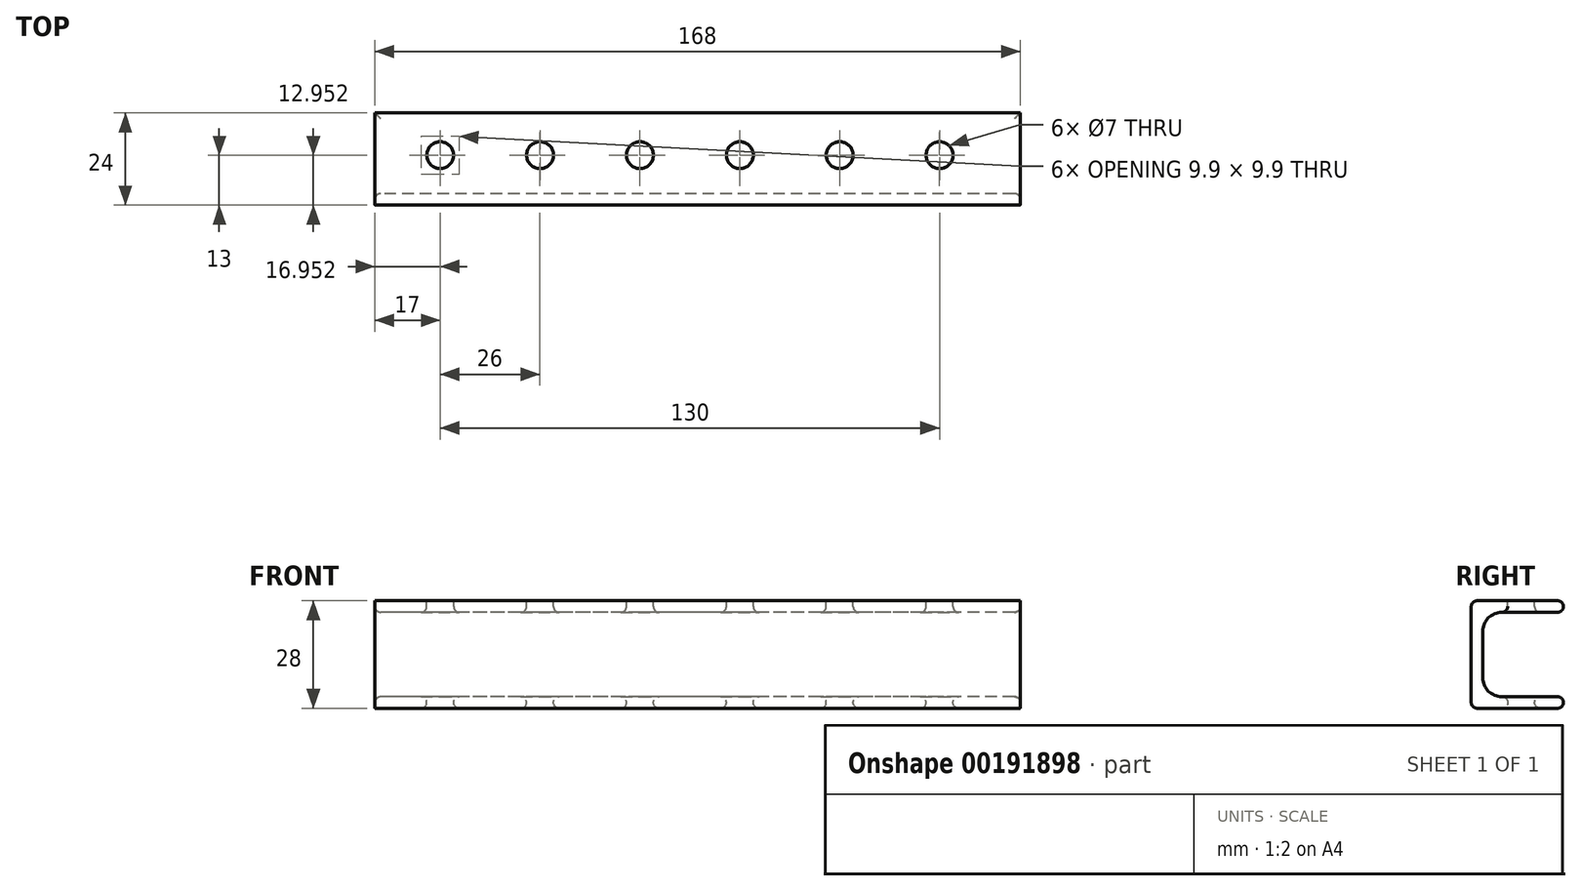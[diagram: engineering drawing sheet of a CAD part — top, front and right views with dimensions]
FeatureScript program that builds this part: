
annotation { "Feature Type Name" : "Feature", "Feature Type Description" : "" }
export const myFeature = defineFeature(function(context is Context, id is Id, definition is map)
    precondition{}
    {
        {
            var Q0;
            Q0=qCreatedBy(makeId("Right.planeOp"),FACE);
            var sketch = newSketch(context, id + "F0", { "sketchPlane" : qUnion([Q0])});
            skLineSegment(sketch, "E0", {"start": v(0, 0) * mm, "end": v(-24, 0) * mm});
            skLineSegment(sketch, "E1", {"start": v(-24, 0) * mm, "end": v(-24, 28) * mm});
            skLineSegment(sketch, "E2", {"start": v(-24, 28) * mm, "end": v(0, 28) * mm});
            skLineSegment(sketch, "E3", {"start": v(0, 28) * mm, "end": v(0, 25) * mm});
            skLineSegment(sketch, "E4", {"start": v(0, 25) * mm, "end": v(-21, 25) * mm});
            skLineSegment(sketch, "E5", {"start": v(-21, 25) * mm, "end": v(-21, 3) * mm});
            skLineSegment(sketch, "E6", {"start": v(-21, 3) * mm, "end": v(0, 3) * mm});
            skLineSegment(sketch, "E7", {"start": v(0, 3) * mm, "end": v(0, 0) * mm});
            skSolve(sketch);
        }
        {
            var Q0;
            Q0=makeQuery(id+"F0.imprint","IMPRINT",FACE,{"disambiguationData":[TD([[makeQuery(id+"F0.imprint","IMPRINT",EDGE,{"derivedFrom":sQuery(id+"F0.wireOp",EDGE,"E0")}),-1.0]])]});
            extrude(context, id + "F1", {"entities" : qUnion([Q0]), "depth" : 168 * mm});
        }
        {
            var Q0;
            Q0=makeQuery(id+"F1.opExtrude","SWEPT_FACE",FACE,{"disambiguationData":[OSD([sQuery(id+"F0.wireOp",EDGE,"E2")])]});
            var sketch = newSketch(context, id + "F2", { "sketchPlane" : qUnion([Q0])});
            skCircle(sketch, "E8", {"center": v(17, -11) * mm, "radius": 3.5 * mm});
            skCircle(sketch, "E9.1.0.0", {"center": v(43, -11) * mm, "radius": 3.5 * mm});
            skCircle(sketch, "E9.2.0.0", {"center": v(69, -11) * mm, "radius": 3.5 * mm});
            skCircle(sketch, "E9.3.0.0", {"center": v(95, -11) * mm, "radius": 3.5 * mm});
            skCircle(sketch, "E9.4.0.0", {"center": v(121, -11) * mm, "radius": 3.5 * mm});
            skCircle(sketch, "E9.5.0.0", {"center": v(147, -11) * mm, "radius": 3.5 * mm});
            skLineSegment(sketch, "E9.direction1", {"start": v(17, -11) * mm, "end": v(43, -11) * mm, "construction": true});
            skSolve(sketch);
        }
        {
            var Q0;
            Q0=makeQuery(id+"F2.imprint","IMPRINT",FACE,{"disambiguationData":[TD([[makeQuery(id+"F2.imprint","IMPRINT",EDGE,{"derivedFrom":sQuery(id+"F2.wireOp",EDGE,"E8")}),1.0]])]});
            var Q1;
            Q1=makeQuery(id+"F2.imprint","IMPRINT",FACE,{"disambiguationData":[TD([[makeQuery(id+"F2.imprint","IMPRINT",EDGE,{"derivedFrom":sQuery(id+"F2.wireOp",EDGE,"E9.1.0.0")}),1.0]])]});
            var Q2;
            Q2=makeQuery(id+"F2.imprint","IMPRINT",FACE,{"disambiguationData":[TD([[makeQuery(id+"F2.imprint","IMPRINT",EDGE,{"derivedFrom":sQuery(id+"F2.wireOp",EDGE,"E9.2.0.0")}),1.0]])]});
            var Q3;
            Q3=makeQuery(id+"F2.imprint","IMPRINT",FACE,{"disambiguationData":[TD([[makeQuery(id+"F2.imprint","IMPRINT",EDGE,{"derivedFrom":sQuery(id+"F2.wireOp",EDGE,"E9.3.0.0")}),1.0]])]});
            var Q4;
            Q4=makeQuery(id+"F2.imprint","IMPRINT",FACE,{"disambiguationData":[TD([[makeQuery(id+"F2.imprint","IMPRINT",EDGE,{"derivedFrom":sQuery(id+"F2.wireOp",EDGE,"E9.4.0.0")}),1.0]])]});
            var Q5;
            Q5=makeQuery(id+"F2.imprint","IMPRINT",FACE,{"disambiguationData":[TD([[makeQuery(id+"F2.imprint","IMPRINT",EDGE,{"derivedFrom":sQuery(id+"F2.wireOp",EDGE,"E9.5.0.0")}),1.0]])]});
            extrude(context, id + "F3", {"entities" : qUnion([Q0, Q1, Q2, Q3, Q4, Q5]), "operationType" : NewBodyOperationType.REMOVE, "oppositeDirection" : true, "depth" : 55 * mm});
        }
        {
            var Q0;
            Q0=makeQuery(id+"F1.opExtrude","SWEPT_EDGE",EDGE,{"disambiguationData":[OSD([sQuery(id+"F0.wireOp",EDGE,"E5"),sQuery(id+"F0.wireOp",EDGE,"E6")])]});
            var Q1;
            Q1=makeQuery(id+"F1.opExtrude","SWEPT_EDGE",EDGE,{"disambiguationData":[OSD([sQuery(id+"F0.wireOp",EDGE,"E4"),sQuery(id+"F0.wireOp",EDGE,"E5")])]});
            fillet(context, id + "F4", {"entities" : qUnion([Q0, Q1]), "radius" : 5 * mm, "tangentPropagation" : true, "allowEdgeOverflow" : false});
        }
        {
            var Q0;
            Q0=makeQuery(id+"F1.opExtrude","SWEPT_EDGE",EDGE,{"disambiguationData":[OSD([sQuery(id+"F0.wireOp",EDGE,"E6"),sQuery(id+"F0.wireOp",EDGE,"E7")])]});
            var Q1;
            Q1=makeQuery(id+"F1.opExtrude","SWEPT_EDGE",EDGE,{"disambiguationData":[OSD([sQuery(id+"F0.wireOp",EDGE,"E0"),sQuery(id+"F0.wireOp",EDGE,"E7")])]});
            var Q2;
            Q2=makeQuery(id+"F1.opExtrude","SWEPT_EDGE",EDGE,{"disambiguationData":[OSD([sQuery(id+"F0.wireOp",EDGE,"E2"),sQuery(id+"F0.wireOp",EDGE,"E3")])]});
            var Q3;
            Q3=makeQuery(id+"F1.opExtrude","SWEPT_EDGE",EDGE,{"disambiguationData":[OSD([sQuery(id+"F0.wireOp",EDGE,"E3"),sQuery(id+"F0.wireOp",EDGE,"E4")])]});
            var Q4;
            Q4=makeQuery(id+"F1.opExtrude","SWEPT_EDGE",EDGE,{"disambiguationData":[OSD([sQuery(id+"F0.wireOp",EDGE,"E1"),sQuery(id+"F0.wireOp",EDGE,"E2")])]});
            var Q5;
            Q5=makeQuery(id+"F1.opExtrude","SWEPT_EDGE",EDGE,{"disambiguationData":[OSD([sQuery(id+"F0.wireOp",EDGE,"E0"),sQuery(id+"F0.wireOp",EDGE,"E1")])]});
            var Q6;
            Q6=makeQuery(id+"F3.boolean.opBoolean","INTERSECT",EDGE,{"derivedFrom":[makeQuery(id+"F1.opExtrude","SWEPT_FACE",FACE,{"disambiguationData":[OSD([sQuery(id+"F0.wireOp",EDGE,"E0")])]}),makeQuery(id+"F3.opExtrude","SWEPT_FACE",FACE,{"disambiguationData":[OSD([sQuery(id+"F2.wireOp",EDGE,"E9.1.0.0")])]})]});
            var Q7;
            Q7=makeQuery(id+"F3.boolean.opBoolean","INTERSECT",EDGE,{"derivedFrom":[makeQuery(id+"F1.opExtrude","SWEPT_FACE",FACE,{"disambiguationData":[OSD([sQuery(id+"F0.wireOp",EDGE,"E0")])]}),makeQuery(id+"F3.opExtrude","SWEPT_FACE",FACE,{"disambiguationData":[OSD([sQuery(id+"F2.wireOp",EDGE,"E8")])]})]});
            var Q8;
            Q8=makeQuery(id+"F3.boolean.opBoolean","INTERSECT",EDGE,{"derivedFrom":[makeQuery(id+"F1.opExtrude","SWEPT_FACE",FACE,{"disambiguationData":[OSD([sQuery(id+"F0.wireOp",EDGE,"E0")])]}),makeQuery(id+"F3.opExtrude","SWEPT_FACE",FACE,{"disambiguationData":[OSD([sQuery(id+"F2.wireOp",EDGE,"E9.2.0.0")])]})]});
            var Q9;
            Q9=makeQuery(id+"F3.boolean.opBoolean","INTERSECT",EDGE,{"derivedFrom":[makeQuery(id+"F1.opExtrude","SWEPT_FACE",FACE,{"disambiguationData":[OSD([sQuery(id+"F0.wireOp",EDGE,"E0")])]}),makeQuery(id+"F3.opExtrude","SWEPT_FACE",FACE,{"disambiguationData":[OSD([sQuery(id+"F2.wireOp",EDGE,"E9.3.0.0")])]})]});
            var Q10;
            Q10=makeQuery(id+"F3.boolean.opBoolean","INTERSECT",EDGE,{"derivedFrom":[makeQuery(id+"F1.opExtrude","SWEPT_FACE",FACE,{"disambiguationData":[OSD([sQuery(id+"F0.wireOp",EDGE,"E0")])]}),makeQuery(id+"F3.opExtrude","SWEPT_FACE",FACE,{"disambiguationData":[OSD([sQuery(id+"F2.wireOp",EDGE,"E9.4.0.0")])]})]});
            var Q11;
            Q11=makeQuery(id+"F3.boolean.opBoolean","INTERSECT",EDGE,{"derivedFrom":[makeQuery(id+"F1.opExtrude","SWEPT_FACE",FACE,{"disambiguationData":[OSD([sQuery(id+"F0.wireOp",EDGE,"E0")])]}),makeQuery(id+"F3.opExtrude","SWEPT_FACE",FACE,{"disambiguationData":[OSD([sQuery(id+"F2.wireOp",EDGE,"E9.5.0.0")])]})]});
            var Q12;
            Q12=makeQuery(id+"F3.boolean.opBoolean","INTERSECT",EDGE,{"derivedFrom":[makeQuery(id+"F1.opExtrude","SWEPT_FACE",FACE,{"disambiguationData":[OSD([sQuery(id+"F0.wireOp",EDGE,"E4")])]}),makeQuery(id+"F3.opExtrude","SWEPT_FACE",FACE,{"disambiguationData":[OSD([sQuery(id+"F2.wireOp",EDGE,"E9.4.0.0")])]})]});
            var Q13;
            Q13=makeQuery(id+"F3.boolean.opBoolean","INTERSECT",EDGE,{"derivedFrom":[makeQuery(id+"F1.opExtrude","SWEPT_FACE",FACE,{"disambiguationData":[OSD([sQuery(id+"F0.wireOp",EDGE,"E4")])]}),makeQuery(id+"F3.opExtrude","SWEPT_FACE",FACE,{"disambiguationData":[OSD([sQuery(id+"F2.wireOp",EDGE,"E9.3.0.0")])]})]});
            var Q14;
            Q14=makeQuery(id+"F3.boolean.opBoolean","INTERSECT",EDGE,{"derivedFrom":[makeQuery(id+"F1.opExtrude","SWEPT_FACE",FACE,{"disambiguationData":[OSD([sQuery(id+"F0.wireOp",EDGE,"E4")])]}),makeQuery(id+"F3.opExtrude","SWEPT_FACE",FACE,{"disambiguationData":[OSD([sQuery(id+"F2.wireOp",EDGE,"E9.2.0.0")])]})]});
            var Q15;
            Q15=makeQuery(id+"F3.boolean.opBoolean","INTERSECT",EDGE,{"derivedFrom":[makeQuery(id+"F1.opExtrude","SWEPT_FACE",FACE,{"disambiguationData":[OSD([sQuery(id+"F0.wireOp",EDGE,"E4")])]}),makeQuery(id+"F3.opExtrude","SWEPT_FACE",FACE,{"disambiguationData":[OSD([sQuery(id+"F2.wireOp",EDGE,"E9.1.0.0")])]})]});
            var Q16;
            Q16=makeQuery(id+"F1.opExtrude","SWEPT_FACE",FACE,{"disambiguationData":[OSD([sQuery(id+"F0.wireOp",EDGE,"E4")])]});
            var Q17;
            Q17=makeQuery(id+"F3.boolean.opBoolean","INTERSECT",EDGE,{"derivedFrom":[makeQuery(id+"F1.opExtrude","SWEPT_FACE",FACE,{"disambiguationData":[OSD([sQuery(id+"F0.wireOp",EDGE,"E6")])]}),makeQuery(id+"F3.opExtrude","SWEPT_FACE",FACE,{"disambiguationData":[OSD([sQuery(id+"F2.wireOp",EDGE,"E8")])]})]});
            var Q18;
            Q18=makeQuery(id+"F3.boolean.opBoolean","INTERSECT",EDGE,{"derivedFrom":[makeQuery(id+"F1.opExtrude","SWEPT_FACE",FACE,{"disambiguationData":[OSD([sQuery(id+"F0.wireOp",EDGE,"E6")])]}),makeQuery(id+"F3.opExtrude","SWEPT_FACE",FACE,{"disambiguationData":[OSD([sQuery(id+"F2.wireOp",EDGE,"E9.1.0.0")])]})]});
            var Q19;
            Q19=makeQuery(id+"F3.boolean.opBoolean","INTERSECT",EDGE,{"derivedFrom":[makeQuery(id+"F1.opExtrude","SWEPT_FACE",FACE,{"disambiguationData":[OSD([sQuery(id+"F0.wireOp",EDGE,"E6")])]}),makeQuery(id+"F3.opExtrude","SWEPT_FACE",FACE,{"disambiguationData":[OSD([sQuery(id+"F2.wireOp",EDGE,"E9.2.0.0")])]})]});
            var Q20;
            Q20=makeQuery(id+"F3.boolean.opBoolean","INTERSECT",EDGE,{"derivedFrom":[makeQuery(id+"F1.opExtrude","SWEPT_FACE",FACE,{"disambiguationData":[OSD([sQuery(id+"F0.wireOp",EDGE,"E6")])]}),makeQuery(id+"F3.opExtrude","SWEPT_FACE",FACE,{"disambiguationData":[OSD([sQuery(id+"F2.wireOp",EDGE,"E9.3.0.0")])]})]});
            var Q21;
            Q21=makeQuery(id+"F3.boolean.opBoolean","INTERSECT",EDGE,{"derivedFrom":[makeQuery(id+"F1.opExtrude","SWEPT_FACE",FACE,{"disambiguationData":[OSD([sQuery(id+"F0.wireOp",EDGE,"E6")])]}),makeQuery(id+"F3.opExtrude","SWEPT_FACE",FACE,{"disambiguationData":[OSD([sQuery(id+"F2.wireOp",EDGE,"E9.4.0.0")])]})]});
            var Q22;
            Q22=makeQuery(id+"F3.boolean.opBoolean","INTERSECT",EDGE,{"derivedFrom":[makeQuery(id+"F1.opExtrude","SWEPT_FACE",FACE,{"disambiguationData":[OSD([sQuery(id+"F0.wireOp",EDGE,"E6")])]}),makeQuery(id+"F3.opExtrude","SWEPT_FACE",FACE,{"disambiguationData":[OSD([sQuery(id+"F2.wireOp",EDGE,"E9.5.0.0")])]})]});
            var Q23;
            Q23=makeQuery(id+"F3.boolean.opBoolean","COPY",EDGE,{"derivedFrom":makeQuery(id+"F3.opExtrude","CAP_EDGE",EDGE,{"disambiguationData":[OSD([sQuery(id+"F2.wireOp",EDGE,"E8")])],"isStart":true})});
            var Q24;
            Q24=makeQuery(id+"F3.boolean.opBoolean","COPY",EDGE,{"derivedFrom":makeQuery(id+"F3.opExtrude","CAP_EDGE",EDGE,{"disambiguationData":[OSD([sQuery(id+"F2.wireOp",EDGE,"E9.1.0.0")])],"isStart":true})});
            var Q25;
            Q25=makeQuery(id+"F3.boolean.opBoolean","COPY",EDGE,{"derivedFrom":makeQuery(id+"F3.opExtrude","CAP_EDGE",EDGE,{"disambiguationData":[OSD([sQuery(id+"F2.wireOp",EDGE,"E9.2.0.0")])],"isStart":true})});
            var Q26;
            Q26=makeQuery(id+"F3.boolean.opBoolean","COPY",EDGE,{"derivedFrom":makeQuery(id+"F3.opExtrude","CAP_EDGE",EDGE,{"disambiguationData":[OSD([sQuery(id+"F2.wireOp",EDGE,"E9.3.0.0")])],"isStart":true})});
            var Q27;
            Q27=makeQuery(id+"F3.boolean.opBoolean","COPY",EDGE,{"derivedFrom":makeQuery(id+"F3.opExtrude","CAP_EDGE",EDGE,{"disambiguationData":[OSD([sQuery(id+"F2.wireOp",EDGE,"E9.4.0.0")])],"isStart":true})});
            var Q28;
            Q28=makeQuery(id+"F3.boolean.opBoolean","COPY",EDGE,{"derivedFrom":makeQuery(id+"F3.opExtrude","CAP_EDGE",EDGE,{"disambiguationData":[OSD([sQuery(id+"F2.wireOp",EDGE,"E9.5.0.0")])],"isStart":true})});
            fillet(context, id + "F5", {"entities" : qUnion([Q0, Q1, Q2, Q3, Q4, Q5, Q6, Q7, Q8, Q9, Q10, Q11, Q12, Q13, Q14, Q15, Q16, Q17, Q18, Q19, Q20, Q21, Q22, Q23, Q24, Q25, Q26, Q27, Q28]), "radius" : 1.5 * mm, "tangentPropagation" : true, "allowEdgeOverflow" : false});
        }
    });
